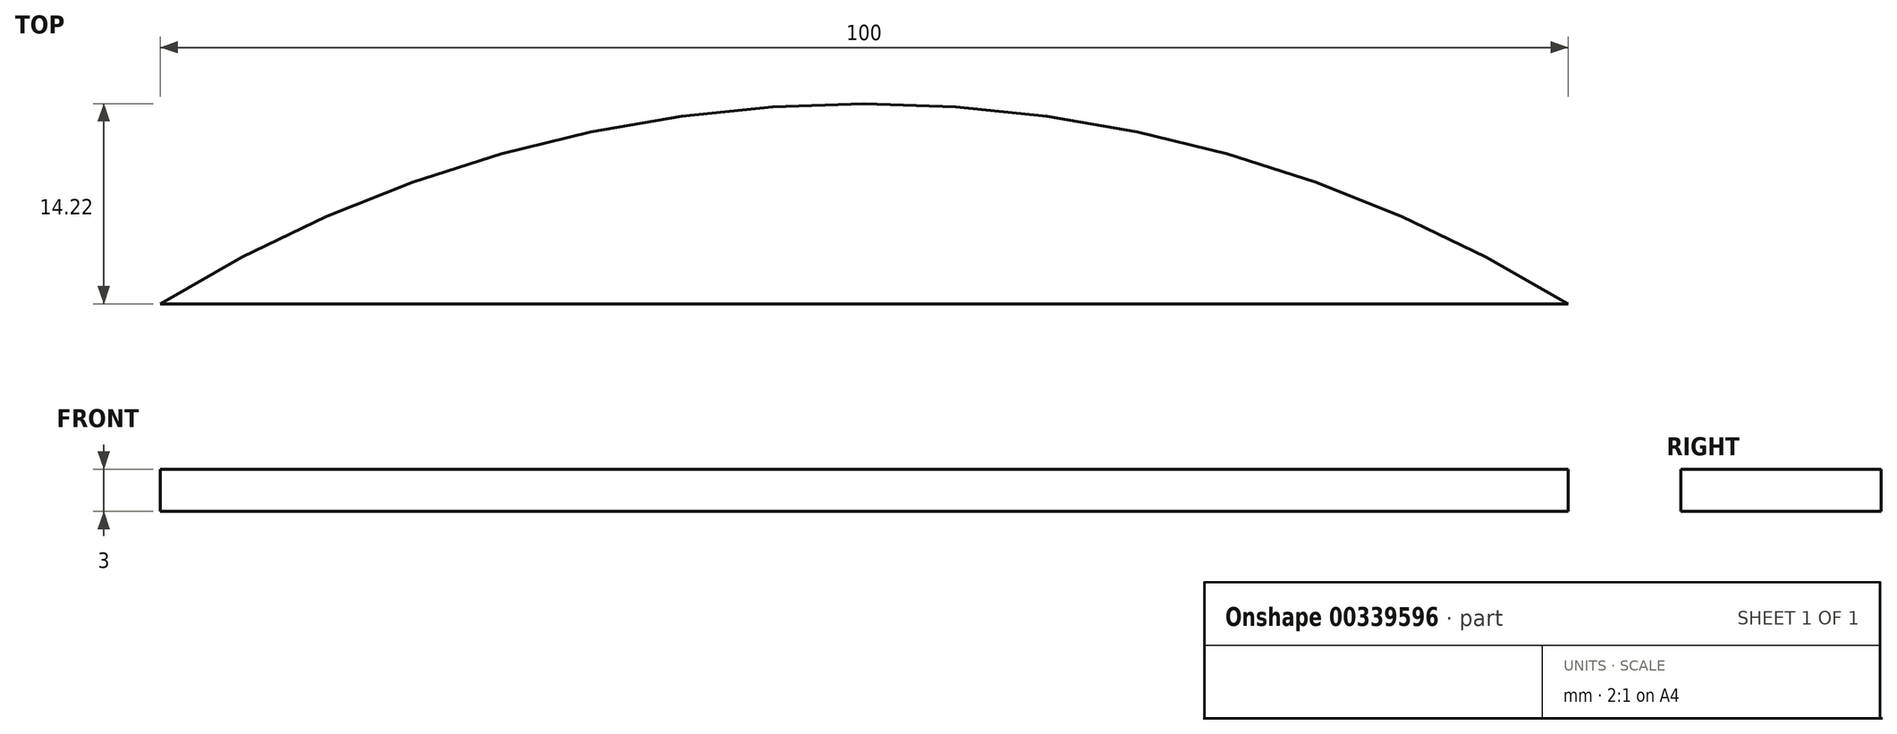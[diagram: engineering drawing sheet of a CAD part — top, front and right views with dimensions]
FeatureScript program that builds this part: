
annotation { "Feature Type Name" : "Feature", "Feature Type Description" : "" }
export const myFeature = defineFeature(function(context is Context, id is Id, definition is map)
    precondition{}
    {
        {
            var Q0;
            Q0=qCreatedBy(makeId("Top.planeOp"),FACE);
            var sketch = newSketch(context, id + "F0", { "sketchPlane" : qUnion([Q0])});
            skCircle(sketch, "E0", {"center": v(-25, 0) * mm, "radius": 95 * mm});
            skCircle(sketch, "E1", {"center": v(25, 0) * mm, "radius": 95 * mm});
            skLineSegment(sketch, "E2", {"start": v(-25, 0) * mm, "end": v(25, 0) * mm});
            skLineSegment(sketch, "E3", {"start": v(-75, 80.78) * mm, "end": v(75, 80.78) * mm});
            skLineSegment(sketch, "E4", {"start": v(-75, -80.78) * mm, "end": v(75, -80.78) * mm});
            skPoint(sketch, "E5", {"position": v(0, 0) * mm});
            skSolve(sketch);
        }
        {
            var Q0;
            {var subQ0=sQuery(id+"F0.wireOp",EDGE,"E3");var subQ1=sQuery(id+"F0.wireOp",EDGE,"E0");var subQ2=makeQuery(id+"F0.imprint","INTERSECT",VERTEX,{"disambiguationData":[OD(0.0)],"derivedFrom":[subQ1,subQ0]});Q0=makeQuery(id+"F0.imprint","IMPRINT",FACE,{"disambiguationData":[TD([[makeQuery(id+"F0.imprint","IMPRINT",EDGE,{"disambiguationData":[TD([[subQ2,-1.0]])],"derivedFrom":subQ1}),1.0]])]});}
            var Q1;
            {var subQ0=sQuery(id+"F0.wireOp",EDGE,"E3");var subQ1=sQuery(id+"F0.wireOp",EDGE,"E0");var subQ2=makeQuery(id+"F0.imprint","INTERSECT",VERTEX,{"disambiguationData":[OD(1.0)],"derivedFrom":[subQ1,subQ0]});Q1=makeQuery(id+"F0.imprint","IMPRINT",FACE,{"disambiguationData":[TD([[makeQuery(id+"F0.imprint","IMPRINT",EDGE,{"disambiguationData":[TD([[subQ2,1.0]])],"derivedFrom":subQ1}),1.0]])]});}
            var Q2;
            {var subQ0=sQuery(id+"F0.wireOp",EDGE,"E3");var subQ1=sQuery(id+"F0.wireOp",EDGE,"E0");var subQ2=makeQuery(id+"F0.imprint","INTERSECT",VERTEX,{"disambiguationData":[OD(1.0)],"derivedFrom":[subQ1,subQ0]});Q2=makeQuery(id+"F0.imprint","IMPRINT",FACE,{"disambiguationData":[TD([[makeQuery(id+"F0.imprint","IMPRINT",EDGE,{"disambiguationData":[TD([[subQ2,1.0]])],"derivedFrom":subQ1}),-1.0]])]});}
            extrude(context, id + "F1", {"entities" : qUnion([Q0, Q1, Q2]), "depth" : 3 * mm});
        }
        {
            var Q0;
            Q0=makeQuery(id+"F1.opExtrude","CAP_FACE",FACE,{"disambiguationData":[OSD([sQuery(id+"F0.wireOp",EDGE,"E0"),sQuery(id+"F0.wireOp",EDGE,"E1"),sQuery(id+"F0.wireOp",EDGE,"E3"),sQuery(id+"F0.wireOp",EDGE,"E4")])],"isStart":false});
            var sketch = newSketch(context, id + "F2", { "sketchPlane" : qUnion([Q0])});
            skLineSegment(sketch, "E6.bottom", {"start": v(-50, 50) * mm, "end": v(50, 50) * mm});
            skLineSegment(sketch, "E6.top", {"start": v(-50, -50) * mm, "end": v(50, -50) * mm});
            skLineSegment(sketch, "E6.left", {"start": v(-50, 50) * mm, "end": v(-50, -50) * mm});
            skLineSegment(sketch, "E6.right", {"start": v(50, 50) * mm, "end": v(50, -50) * mm});
            skLineSegment(sketch, "E7", {"start": v(-50, 50) * mm, "end": v(50, -50) * mm});
            skPoint(sketch, "E8", {"position": v(0, 0) * mm});
            skSolve(sketch);
        }
        {
            var Q0;
            Q0=sQuery(id+"F2.wireOp",VERTEX,"E6.left.start");
            var Q1;
            Q1=sQuery(id+"F2.wireOp",VERTEX,"E6.right.start");
            var Q2;
            Q2=sQuery(id+"F2.wireOp",VERTEX,"E6.top.end");
            var Q3;
            Q3=sQuery(id+"F2.wireOp",VERTEX,"E6.left.end");
            var Q4;
            Q4=makeQuery(id+"F1.opExtrude","SWEPT_BODY",BODY,{"disambiguationData":[OSD([sQuery(id+"F0.wireOp",EDGE,"E0"),sQuery(id+"F0.wireOp",EDGE,"E1"),sQuery(id+"F0.wireOp",EDGE,"E3"),sQuery(id+"F0.wireOp",EDGE,"E4")])]});
            hole(context, id + "F3", {"style" : HoleStyle.SIMPLE, "holeDiameter" : 3 * mm, "endStyle" : HoleEndStyle.THROUGH, "locations" : qUnion([Q0, Q1, Q2, Q3]), "scope" : qUnion([Q4])});
        }
        {
            var Q0;
            Q0=makeQuery(id+"F1.opExtrude","CAP_FACE",FACE,{"disambiguationData":[OSD([sQuery(id+"F0.wireOp",EDGE,"E0"),sQuery(id+"F0.wireOp",EDGE,"E1"),sQuery(id+"F0.wireOp",EDGE,"E3"),sQuery(id+"F0.wireOp",EDGE,"E4")])],"isStart":false});
            var sketch = newSketch(context, id + "F4", { "sketchPlane" : qUnion([Q0])});
            skCircle(sketch, "E9", {"center": v(0, 0) * mm, "radius": 40 * mm});
            skCircle(sketch, "E10", {"center": v(0, 0) * mm, "radius": 30 * mm});
            skLineSegment(sketch, "E11.bottom", {"start": v(-21.21, 21.21) * mm, "end": v(21.21, 21.21) * mm});
            skLineSegment(sketch, "E11.top", {"start": v(-21.21, -21.21) * mm, "end": v(21.21, -21.21) * mm});
            skLineSegment(sketch, "E11.left", {"start": v(-21.21, 21.21) * mm, "end": v(-21.21, -21.21) * mm});
            skLineSegment(sketch, "E11.right", {"start": v(21.21, 21.21) * mm, "end": v(21.21, -21.21) * mm});
            skSolve(sketch);
        }
        {
            var Q0;
            Q0=sQuery(id+"F4.wireOp",VERTEX,"E11.bottom.start");
            var Q1;
            Q1=sQuery(id+"F4.wireOp",VERTEX,"E11.right.start");
            var Q2;
            Q2=sQuery(id+"F4.wireOp",VERTEX,"E11.top.end");
            var Q3;
            Q3=sQuery(id+"F4.wireOp",VERTEX,"E11.left.end");
            var Q4;
            Q4=makeQuery(id+"F1.opExtrude","SWEPT_BODY",BODY,{"disambiguationData":[OSD([sQuery(id+"F0.wireOp",EDGE,"E0"),sQuery(id+"F0.wireOp",EDGE,"E1"),sQuery(id+"F0.wireOp",EDGE,"E3"),sQuery(id+"F0.wireOp",EDGE,"E4")])]});
            hole(context, id + "F5", {"style" : HoleStyle.SIMPLE, "holeDiameter" : 3 * mm, "endStyle" : HoleEndStyle.THROUGH, "locations" : qUnion([Q0, Q1, Q2, Q3]), "scope" : qUnion([Q4])});
        }
        {
            var Q0;
            Q0=makeQuery(id+"F1.opExtrude","CAP_FACE",FACE,{"disambiguationData":[OSD([sQuery(id+"F0.wireOp",EDGE,"E0"),sQuery(id+"F0.wireOp",EDGE,"E1"),sQuery(id+"F0.wireOp",EDGE,"E3"),sQuery(id+"F0.wireOp",EDGE,"E4")])],"isStart":true});
            var sketch = newSketch(context, id + "F6", { "sketchPlane" : qUnion([Q0])});
            skLineSegment(sketch, "E12.bottom", {"start": v(-28, 45) * mm, "end": v(28, 45) * mm});
            skLineSegment(sketch, "E12.top", {"start": v(-28, -40) * mm, "end": v(28, -40) * mm});
            skLineSegment(sketch, "E12.left", {"start": v(-28, 45) * mm, "end": v(-28, -40) * mm});
            skLineSegment(sketch, "E12.right", {"start": v(28, 45) * mm, "end": v(28, -40) * mm});
            skPoint(sketch, "E13", {"position": v(0, 0) * mm});
            skLineSegment(sketch, "E14.bottom", {"start": v(24.5, 41.5) * mm, "end": v(-24.5, 41.5) * mm});
            skLineSegment(sketch, "E14.top", {"start": v(24.5, -16.5) * mm, "end": v(-24.5, -16.5) * mm});
            skLineSegment(sketch, "E14.left", {"start": v(24.5, 41.5) * mm, "end": v(24.5, -16.5) * mm});
            skLineSegment(sketch, "E14.right", {"start": v(-24.5, 41.5) * mm, "end": v(-24.5, -16.5) * mm});
            skPoint(sketch, "E15", {"position": v(0, 41.5) * mm});
            skLineSegment(sketch, "E16", {"start": v(0, 0) * mm, "end": v(0, 41.5) * mm});
            skLineSegment(sketch, "E17", {"start": v(0, 0) * mm, "end": v(0, 45) * mm});
            skSolve(sketch);
        }
        {
            var Q0;
            Q0=sQuery(id+"F6.wireOp",VERTEX,"E14.right.start");
            var Q1;
            Q1=sQuery(id+"F6.wireOp",VERTEX,"E14.bottom.start");
            var Q2;
            Q2=sQuery(id+"F6.wireOp",VERTEX,"E14.left.end");
            var Q3;
            Q3=sQuery(id+"F6.wireOp",VERTEX,"E14.right.end");
            var Q4;
            Q4=makeQuery(id+"F1.opExtrude","SWEPT_BODY",BODY,{"disambiguationData":[OSD([sQuery(id+"F0.wireOp",EDGE,"E0"),sQuery(id+"F0.wireOp",EDGE,"E1"),sQuery(id+"F0.wireOp",EDGE,"E3"),sQuery(id+"F0.wireOp",EDGE,"E4")])]});
            hole(context, id + "F7", {"style" : HoleStyle.SIMPLE, "holeDiameter" : 3 * mm, "endStyle" : HoleEndStyle.THROUGH, "locations" : qUnion([Q0, Q1, Q2, Q3]), "scope" : qUnion([Q4])});
        }
        {
            var Q0;
            Q0=makeQuery(id+"F1.opExtrude","CAP_FACE",FACE,{"disambiguationData":[OSD([sQuery(id+"F0.wireOp",EDGE,"E0"),sQuery(id+"F0.wireOp",EDGE,"E1"),sQuery(id+"F0.wireOp",EDGE,"E3"),sQuery(id+"F0.wireOp",EDGE,"E4")])],"isStart":false});
            var sketch = newSketch(context, id + "F8", { "sketchPlane" : qUnion([Q0])});
            skLineSegment(sketch, "E18", {"start": v(0, 0) * mm, "end": v(-80, 0) * mm});
            skSolve(sketch);
        }
        {
            var Q0;
            Q0=sQuery(id+"F8.wireOp",VERTEX,"E18.end");
            var Q1;
            Q1=makeQuery(id+"F1.opExtrude","SWEPT_BODY",BODY,{"disambiguationData":[OSD([sQuery(id+"F0.wireOp",EDGE,"E0"),sQuery(id+"F0.wireOp",EDGE,"E1"),sQuery(id+"F0.wireOp",EDGE,"E3"),sQuery(id+"F0.wireOp",EDGE,"E4")])]});
            hole(context, id + "F9", {"style" : HoleStyle.SIMPLE, "holeDiameter" : 16 * mm, "endStyle" : HoleEndStyle.THROUGH, "locations" : qUnion([Q0]), "scope" : qUnion([Q1]), "isTappedThrough" : true});
        }
    });
